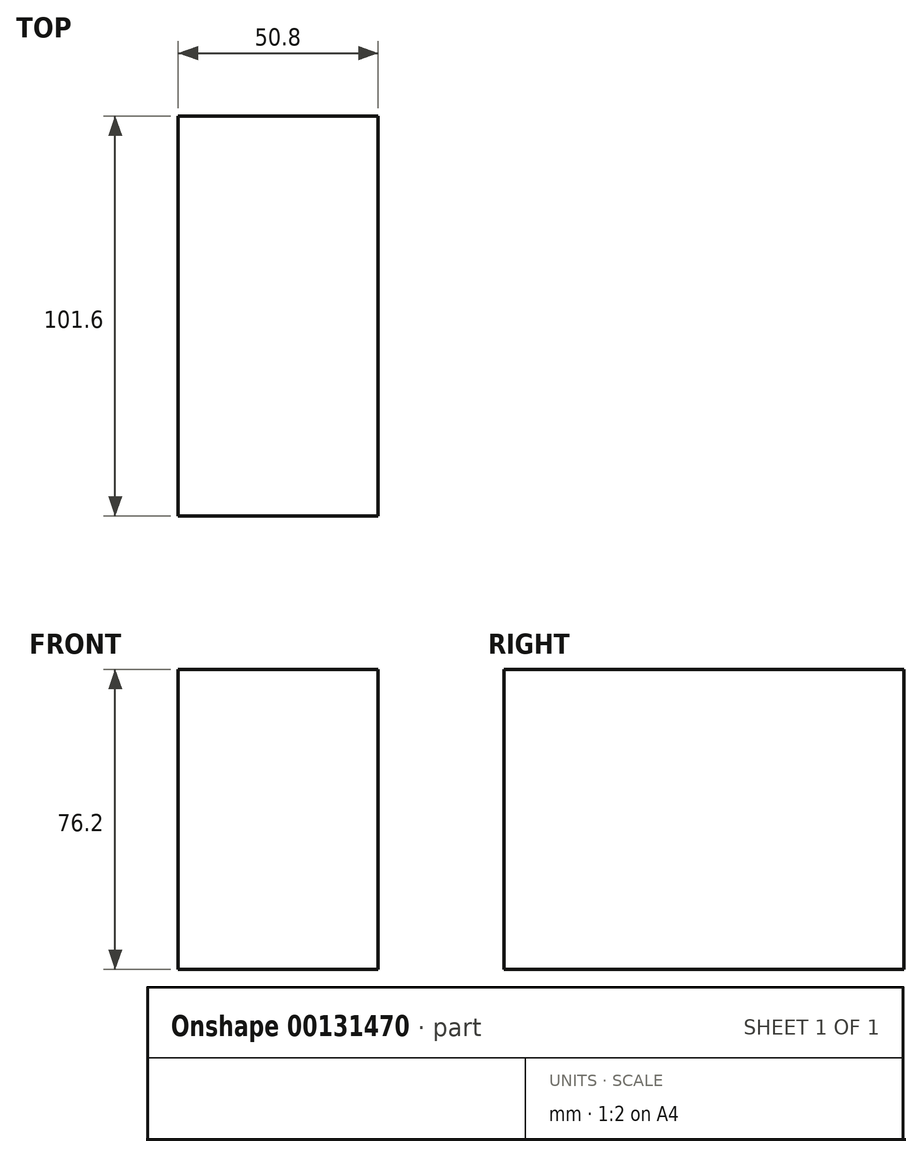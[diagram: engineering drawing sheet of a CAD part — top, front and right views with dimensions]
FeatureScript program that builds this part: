
annotation { "Feature Type Name" : "Feature", "Feature Type Description" : "" }
export const myFeature = defineFeature(function(context is Context, id is Id, definition is map)
    precondition{}
    {
        {
            var Q0;
            Q0=qCreatedBy(makeId("Front.planeOp"),FACE);
            var sketch = newSketch(context, id + "F0", { "sketchPlane" : qUnion([Q0])});
            skLineSegment(sketch, "E0.bottom", {"start": v(24.82, 62.35) * mm, "end": v(-25.98, 62.35) * mm});
            skLineSegment(sketch, "E0.top", {"start": v(24.82, -13.85) * mm, "end": v(-25.98, -13.85) * mm});
            skLineSegment(sketch, "E0.left", {"start": v(24.82, 62.35) * mm, "end": v(24.82, -13.85) * mm});
            skLineSegment(sketch, "E0.right", {"start": v(-25.98, 62.35) * mm, "end": v(-25.98, -13.85) * mm});
            skSolve(sketch);
        }
        {
            var Q0;
            Q0 = qSketchRegion(id + "F0", true);
            extrude(context, id + "F1", {"entities" : qUnion([Q0]), "endBound" : BoundingType.SYMMETRIC, "depth" : 101.6 * mm});
        }
    });
